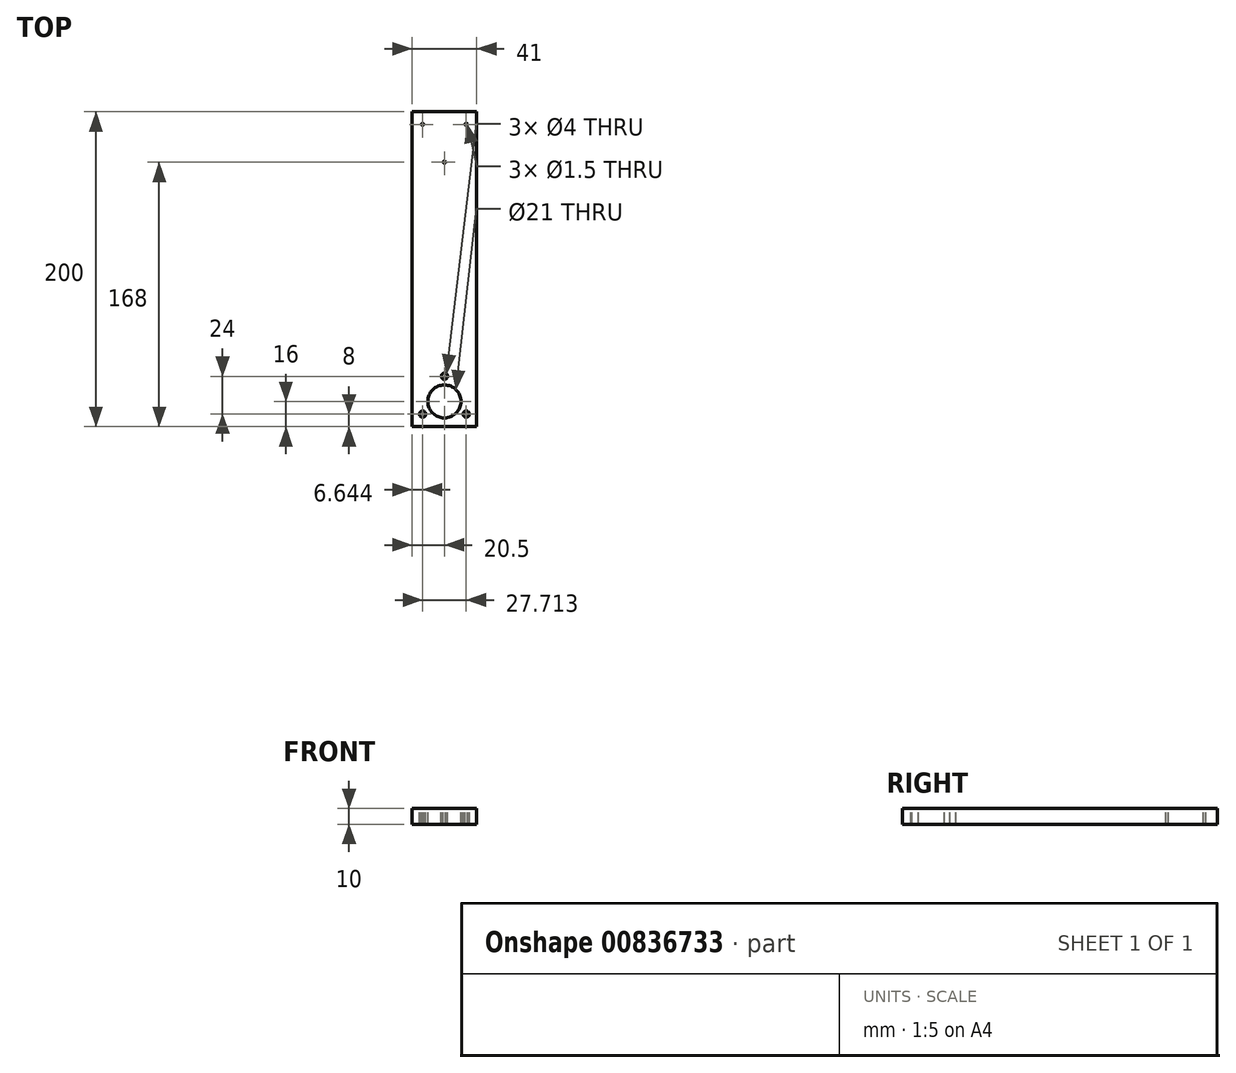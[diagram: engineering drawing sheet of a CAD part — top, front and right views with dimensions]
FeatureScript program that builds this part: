
annotation { "Feature Type Name" : "Feature", "Feature Type Description" : "" }
export const myFeature = defineFeature(function(context is Context, id is Id, definition is map)
    precondition{}
    {
        {
            var Q0;
            Q0=qCreatedBy(makeId("Top.planeOp"),FACE);
            var sketch = newSketch(context, id + "F0", { "sketchPlane" : qUnion([Q0])});
            skLineSegment(sketch, "E0.bottom", {"start": v(20.5, -100) * mm, "end": v(-20.5, -100) * mm});
            skLineSegment(sketch, "E0.top", {"start": v(20.5, 100) * mm, "end": v(-20.5, 100) * mm});
            skLineSegment(sketch, "E0.left", {"start": v(20.5, -100) * mm, "end": v(20.5, 100) * mm});
            skLineSegment(sketch, "E0.right", {"start": v(-20.5, -100) * mm, "end": v(-20.5, 100) * mm});
            skPoint(sketch, "E0.middle", {"position": v(0, 0) * mm});
            skSolve(sketch);
        }
        {
            var Q0;
            Q0 = qSketchRegion(id + "F0", true);
            extrude(context, id + "F1", {"entities" : qUnion([Q0]), "depth" : 10 * mm, "offsetDistance" : 25 * mm});
        }
        {
            var Q0;
            Q0=makeQuery(id+"F1.opExtrude","CAP_FACE",FACE,{"disambiguationData":[OSD([sQuery(id+"F0.wireOp",EDGE,"E0.bottom"),sQuery(id+"F0.wireOp",EDGE,"E0.top"),sQuery(id+"F0.wireOp",EDGE,"E0.left"),sQuery(id+"F0.wireOp",EDGE,"E0.right")])],"isStart":false});
            var sketch = newSketch(context, id + "F2", { "sketchPlane" : qUnion([Q0])});
            skCircle(sketch, "E1", {"center": v(0, -84) * mm, "radius": 16 * mm, "construction": true});
            skCircle(sketch, "E2", {"center": v(0, -68) * mm, "radius": 2 * mm});
            skLineSegment(sketch, "E3", {"start": v(0, -68) * mm, "end": v(-13.86, -92) * mm, "construction": true});
            skLineSegment(sketch, "E4", {"start": v(-13.86, -92) * mm, "end": v(13.86, -92) * mm, "construction": true});
            skLineSegment(sketch, "E5", {"start": v(13.86, -92) * mm, "end": v(0, -68) * mm, "construction": true});
            skCircle(sketch, "E6", {"center": v(-13.86, -92) * mm, "radius": 2 * mm});
            skCircle(sketch, "E7", {"center": v(13.86, -92) * mm, "radius": 2 * mm});
            skCircle(sketch, "E8", {"center": v(0, 84) * mm, "radius": 16 * mm, "construction": true});
            skLineSegment(sketch, "E9", {"start": v(0, 84) * mm, "end": v(0, 84) * mm});
            skCircle(sketch, "E10", {"center": v(0, 68) * mm, "radius": 0.75 * mm});
            skLineSegment(sketch, "E11", {"start": v(0, 68) * mm, "end": v(-13.86, 92) * mm, "construction": true});
            skLineSegment(sketch, "E12", {"start": v(-13.86, 92) * mm, "end": v(13.86, 92) * mm, "construction": true});
            skLineSegment(sketch, "E13", {"start": v(13.86, 92) * mm, "end": v(0, 68) * mm, "construction": true});
            skCircle(sketch, "E14", {"center": v(-13.86, 92) * mm, "radius": 0.75 * mm});
            skCircle(sketch, "E15", {"center": v(13.86, 92) * mm, "radius": 0.75 * mm});
            skCircle(sketch, "E16", {"center": v(0, -84) * mm, "radius": 10.5 * mm});
            skSolve(sketch);
        }
        {
            var Q0;
            Q0 = qSketchRegion(id + "F2", true);
            extrude(context, id + "F3", {"entities" : qUnion([Q0]), "operationType" : NewBodyOperationType.REMOVE, "oppositeDirection" : true, "depth" : 25 * mm, "offsetDistance" : 25 * mm});
        }
        {
            var Q0;
            Q0 = qSketchRegion(id + "F2", true);
            extrude(context, id + "F4", {"entities" : qUnion([Q0]), "operationType" : NewBodyOperationType.REMOVE, "oppositeDirection" : true, "depth" : 25 * mm, "offsetDistance" : 25 * mm});
        }
    });
